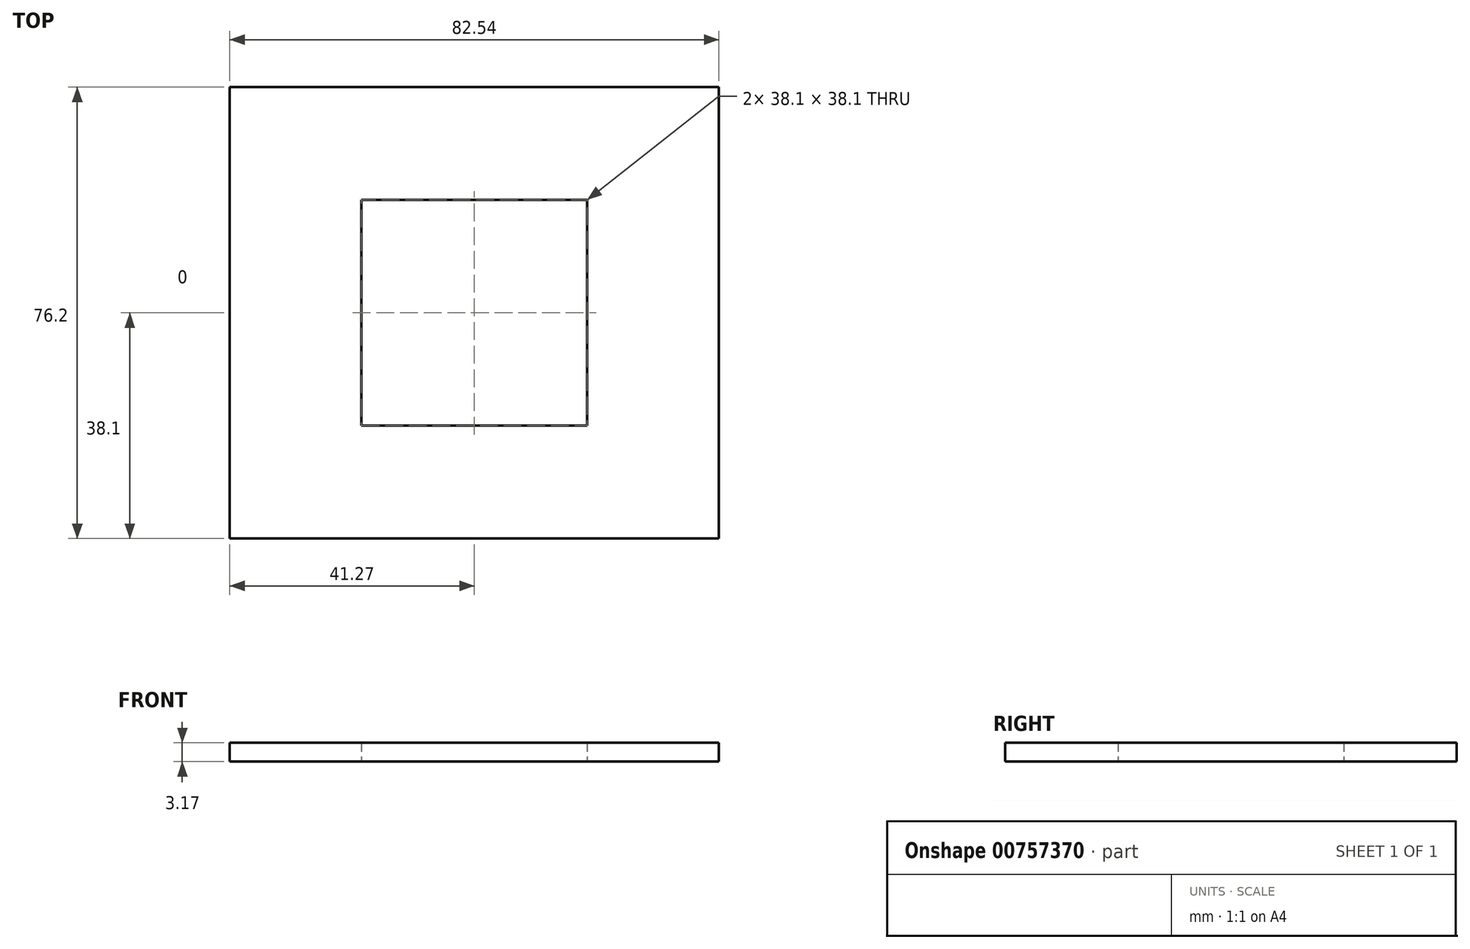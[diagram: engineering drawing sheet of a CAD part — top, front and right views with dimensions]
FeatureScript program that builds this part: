
annotation { "Feature Type Name" : "Feature", "Feature Type Description" : "" }
export const myFeature = defineFeature(function(context is Context, id is Id, definition is map)
    precondition{}
    {
        {
            var Q0;
            Q0=qCreatedBy(makeId("Top.planeOp"),FACE);
            var sketch = newSketch(context, id + "F0", { "sketchPlane" : qUnion([Q0])});
            skLineSegment(sketch, "E0.bottom", {"start": v(-41.28, -38.1) * mm, "end": v(41.28, -38.1) * mm});
            skLineSegment(sketch, "E0.top", {"start": v(-41.28, 38.1) * mm, "end": v(41.28, 38.1) * mm});
            skLineSegment(sketch, "E0.left", {"start": v(-41.28, -38.1) * mm, "end": v(-41.28, 38.1) * mm});
            skLineSegment(sketch, "E0.right", {"start": v(41.28, -38.1) * mm, "end": v(41.28, 38.1) * mm});
            skPoint(sketch, "E0.middle", {"position": v(0, 0) * mm});
            skSolve(sketch);
        }
        {
            var Q0;
            Q0=qSketchRegion(id+"F0",true);
            extrude(context, id + "F1", {"entities" : qUnion([Q0]), "depth" : 3.17 * mm, "offsetDistance" : 25.4 * mm});
        }
        {
            var Q0;
            Q0=makeQuery(id+"F1.opExtrude","CAP_FACE",FACE,{"disambiguationData":[OSD([sQuery(id+"F0.wireOp",EDGE,"E0.bottom"),sQuery(id+"F0.wireOp",EDGE,"E0.top"),sQuery(id+"F0.wireOp",EDGE,"E0.left"),sQuery(id+"F0.wireOp",EDGE,"E0.right")])],"isStart":true});
            var sketch = newSketch(context, id + "F2", { "sketchPlane" : qUnion([Q0])});
            skLineSegment(sketch, "E1.bottom", {"start": v(19.05, 19.05) * mm, "end": v(-19.05, 19.05) * mm});
            skLineSegment(sketch, "E1.top", {"start": v(19.05, -19.05) * mm, "end": v(-19.05, -19.05) * mm});
            skLineSegment(sketch, "E1.left", {"start": v(19.05, 19.05) * mm, "end": v(19.05, -19.05) * mm});
            skLineSegment(sketch, "E1.right", {"start": v(-19.05, 19.05) * mm, "end": v(-19.05, -19.05) * mm});
            skPoint(sketch, "E1.middle", {"position": v(0, 0) * mm});
            skSolve(sketch);
        }
        {
            var Q0;
            Q0=makeQuery(id+"F2.imprint","IMPRINT",FACE,{"disambiguationData":[TD([[makeQuery(id+"F2.imprint","IMPRINT",EDGE,{"derivedFrom":sQuery(id+"F2.wireOp",EDGE,"E1.bottom")}),1.0]])]});
            extrude(context, id + "F3", {"entities" : qUnion([Q0]), "operationType" : NewBodyOperationType.REMOVE, "oppositeDirection" : true, "depth" : 3.17 * mm, "offsetDistance" : 25.4 * mm});
        }
    });
